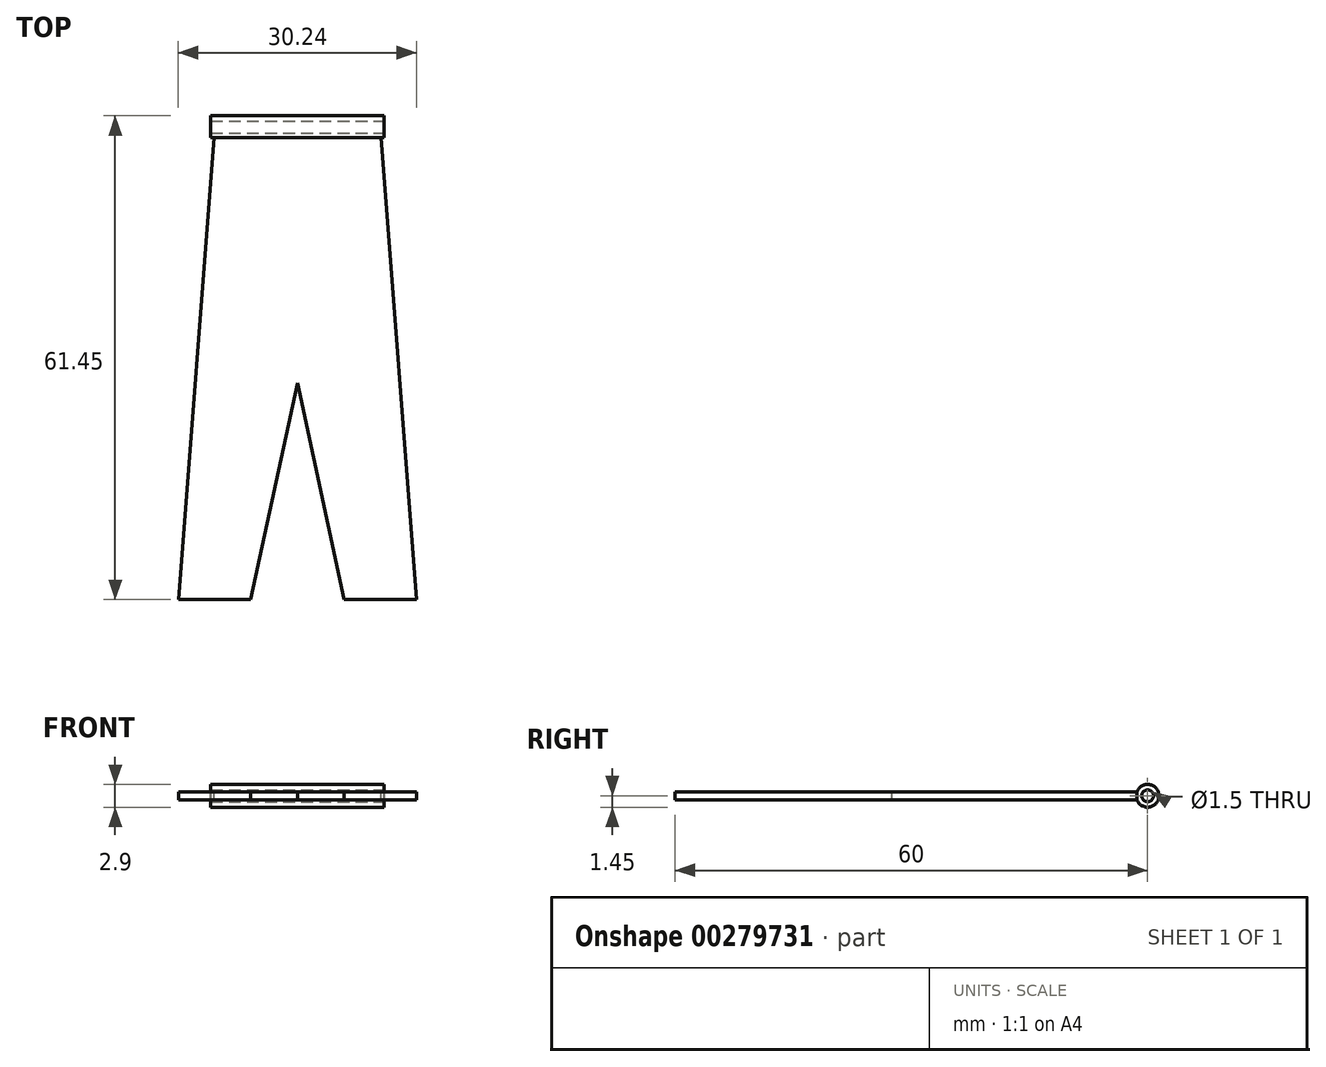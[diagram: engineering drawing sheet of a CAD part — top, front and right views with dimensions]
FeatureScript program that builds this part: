
annotation { "Feature Type Name" : "Feature", "Feature Type Description" : "" }
export const myFeature = defineFeature(function(context is Context, id is Id, definition is map)
    precondition{}
    {
        {
            var Q0;
            Q0=qCreatedBy(makeId("Right.planeOp"),FACE);
            var sketch = newSketch(context, id + "F0", { "sketchPlane" : qUnion([Q0])});
            skCircle(sketch, "E0", {"center": v(0, 0) * mm, "radius": 1.45 * mm});
            skSolve(sketch);
        }
        {
            var Q0;
            Q0 = qSketchRegion(id + "F0", true);
            extrude(context, id + "F1", {"entities" : qUnion([Q0]), "depth" : 24 * mm});
        }
        {
            var Q0;
            Q0=qCreatedBy(makeId("Front.planeOp"),FACE);
            var sketch = newSketch(context, id + "F2", { "sketchPlane" : qUnion([Q0])});
            skLineSegment(sketch, "E1", {"start": v(1.5, 0.5) * mm, "end": v(22.5, 0.5) * mm});
            skLineSegment(sketch, "E2", {"start": v(22.5, 0.5) * mm, "end": v(22.5, -0.5) * mm});
            skLineSegment(sketch, "E3", {"start": v(22.5, -0.5) * mm, "end": v(1.5, -0.5) * mm});
            skLineSegment(sketch, "E4", {"start": v(1.5, 0.5) * mm, "end": v(1.5, -0.5) * mm});
            skSolve(sketch);
        }
        {
            var Q0;
            Q0=qCreatedBy(makeId("Front.planeOp"),FACE);
            cPlane(context, id + "F3", {"entities" : qUnion([Q0]), "cplaneType" : CPlaneType.OFFSET, "offset" : 65 * mm, "width" : 150 * mm, "height" : 150 * mm});
        }
        {
            var Q0;
            Q0=qCreatedBy(id+"F3.planeOp",FACE);
            var sketch = newSketch(context, id + "F4", { "sketchPlane" : qUnion([Q0])});
            skLineSegment(sketch, "E5.0", {"start": v(1.5, 0.5) * mm, "end": v(22.5, 0.5) * mm});
            skLineSegment(sketch, "E6.0", {"start": v(22.5, -0.5) * mm, "end": v(1.5, -0.5) * mm});
            skLineSegment(sketch, "E7", {"start": v(1.5, 0.5) * mm, "end": v(-3.5, 0.5) * mm});
            skLineSegment(sketch, "E8", {"start": v(-3.5, 0.5) * mm, "end": v(-3.5, -0.5) * mm});
            skLineSegment(sketch, "E9", {"start": v(-3.5, -0.5) * mm, "end": v(1.5, -0.5) * mm});
            skLineSegment(sketch, "E10", {"start": v(22.5, 0.5) * mm, "end": v(27.5, 0.5) * mm});
            skLineSegment(sketch, "E11", {"start": v(27.5, 0.5) * mm, "end": v(27.5, -0.5) * mm});
            skLineSegment(sketch, "E12", {"start": v(27.5, -0.5) * mm, "end": v(22.5, -0.5) * mm});
            skSolve(sketch);
        }
        {
            var Q0;
            Q0 = qSketchRegion(id + "F4", true);
            extrude(context, id + "F5", {"entities" : qUnion([Q0]), "operationType" : NewBodyOperationType.ADD, "oppositeDirection" : true, "depth" : 65 * mm});
        }
        {
            var Q0;
            Q0=makeQuery(id+"F5.opExtrude","SWEPT_FACE",FACE,{"disambiguationData":[OSD([sQuery(id+"F4.wireOp",EDGE,"E5.0"),sQuery(id+"F4.wireOp",EDGE,"E7"),sQuery(id+"F4.wireOp",EDGE,"E10")])]});
            var sketch = newSketch(context, id + "F6", { "sketchPlane" : qUnion([Q0])});
            skPoint(sketch, "E13.0", {"position": v(1.5, 0) * mm});
            skPoint(sketch, "E14.0", {"position": v(22.5, 0) * mm});
            skLineSegment(sketch, "E15.0", {"start": v(27.5, 0) * mm, "end": v(27.5, -65) * mm});
            skLineSegment(sketch, "E16.0", {"start": v(-3.5, 0) * mm, "end": v(-3.5, -65) * mm});
            skLineSegment(sketch, "E17", {"start": v(0, 0) * mm, "end": v(-3.5, 0) * mm});
            skLineSegment(sketch, "E18", {"start": v(24, 0) * mm, "end": v(27.5, 0) * mm});
            skLineSegment(sketch, "E19", {"start": v(22.6, -1.36) * mm, "end": v(27.5, -65) * mm});
            skLineSegment(sketch, "E20", {"start": v(-3.5, -65) * mm, "end": v(1.4, -1.36) * mm});
            skLineSegment(sketch, "E21", {"start": v(0, 0) * mm, "end": v(0, -1.36) * mm});
            skLineSegment(sketch, "E22", {"start": v(0, -1.36) * mm, "end": v(1.4, -1.36) * mm});
            skLineSegment(sketch, "E23", {"start": v(24, 0) * mm, "end": v(24, -1.36) * mm});
            skLineSegment(sketch, "E24", {"start": v(24, -1.36) * mm, "end": v(22.6, -1.36) * mm});
            skLineSegment(sketch, "E25", {"start": v(12, -65) * mm, "end": v(5, -65) * mm});
            skLineSegment(sketch, "E26", {"start": v(5, -65) * mm, "end": v(12, -32.5) * mm});
            skPoint(sketch, "E26.endSnap0", {"position": v(-3.5, -32.5) * mm});
            skPoint(sketch, "E26.endSnap1", {"position": v(12, -1.36) * mm});
            skLineSegment(sketch, "E27", {"start": v(12, -32.5) * mm, "end": v(19, -65) * mm});
            skLineSegment(sketch, "E28", {"start": v(12, -65) * mm, "end": v(19, -65) * mm});
            skSolve(sketch);
        }
        {
            var Q0;
            Q0 = qSketchRegion(id + "F6", true);
            extrude(context, id + "F7", {"entities" : qUnion([Q0]), "operationType" : NewBodyOperationType.REMOVE, "oppositeDirection" : true, "depth" : 25 * mm});
        }
        {
            var Q0;
            Q0=makeQuery(id+"F5.opExtrude","SWEPT_FACE",FACE,{"disambiguationData":[OSD([sQuery(id+"F4.wireOp",EDGE,"E5.0"),sQuery(id+"F4.wireOp",EDGE,"E7"),sQuery(id+"F4.wireOp",EDGE,"E10")])]});
            var sketch = newSketch(context, id + "F8", { "sketchPlane" : qUnion([Q0])});
            skLineSegment(sketch, "E29", {"start": v(-3.5, -65) * mm, "end": v(-3.5, -60) * mm});
            skLineSegment(sketch, "E30", {"start": v(-3.5, -60) * mm, "end": v(27.5, -60) * mm});
            skLineSegment(sketch, "E31", {"start": v(27.5, -60) * mm, "end": v(27.5, -65) * mm});
            skLineSegment(sketch, "E32", {"start": v(27.5, -65) * mm, "end": v(-3.5, -65) * mm});
            skSolve(sketch);
        }
        {
            var Q0;
            Q0 = qSketchRegion(id + "F8", true);
            extrude(context, id + "F9", {"entities" : qUnion([Q0]), "operationType" : NewBodyOperationType.REMOVE, "oppositeDirection" : true, "depth" : 25 * mm});
        }
        {
            var Q0;
            Q0=makeQuery(id+"F7.boolean.opBoolean","MERGE",FACE,{"derivedFrom":[makeQuery(id+"F1.opExtrude","CAP_FACE",FACE,{"disambiguationData":[OSD([sQuery(id+"F0.wireOp",EDGE,"E0")])],"isStart":false}),makeQuery(id+"F7.opExtrude","SWEPT_FACE",FACE,{"disambiguationData":[OSD([sQuery(id+"F6.wireOp",EDGE,"E23")])]})]});
            var sketch = newSketch(context, id + "F10", { "sketchPlane" : qUnion([Q0])});
            skPoint(sketch, "E33.0", {"position": v(0, 0) * mm});
            skCircle(sketch, "E34", {"center": v(0, 0) * mm, "radius": 0.75 * mm});
            skSolve(sketch);
        }
        {
            var Q0;
            Q0 = qSketchRegion(id + "F10", true);
            extrude(context, id + "F11", {"entities" : qUnion([Q0]), "operationType" : NewBodyOperationType.REMOVE, "oppositeDirection" : true, "depth" : 40 * mm});
        }
        {
            var Q0;
            Q0=qCreatedBy(makeId("Top.planeOp"),FACE);
            var sketch = newSketch(context, id + "F12", { "sketchPlane" : qUnion([Q0])});
            skLineSegment(sketch, "E35", {"start": v(1, 1.45) * mm, "end": v(0, 1.45) * mm});
            skLineSegment(sketch, "E36", {"start": v(0, 1.45) * mm, "end": v(0, -1.45) * mm});
            skLineSegment(sketch, "E37", {"start": v(0, -1.45) * mm, "end": v(1, -1.45) * mm});
            skLineSegment(sketch, "E38", {"start": v(1, -1.45) * mm, "end": v(1, 1.45) * mm});
            skPoint(sketch, "E39.0", {"position": v(24, 1.45) * mm});
            skLineSegment(sketch, "E40", {"start": v(24, 1.45) * mm, "end": v(23, 1.45) * mm});
            skLineSegment(sketch, "E41", {"start": v(23, 1.45) * mm, "end": v(23, -1.57) * mm});
            skLineSegment(sketch, "E42", {"start": v(23, -1.57) * mm, "end": v(24, -1.57) * mm});
            skLineSegment(sketch, "E43", {"start": v(24, -1.57) * mm, "end": v(24, 1.45) * mm});
            skSolve(sketch);
        }
        {
            var Q0;
            Q0 = qSketchRegion(id + "F12", true);
            extrude(context, id + "F13", {"entities" : qUnion([Q0]), "operationType" : NewBodyOperationType.REMOVE, "endBound" : BoundingType.SYMMETRIC, "depth" : 25 * mm});
        }
    });
